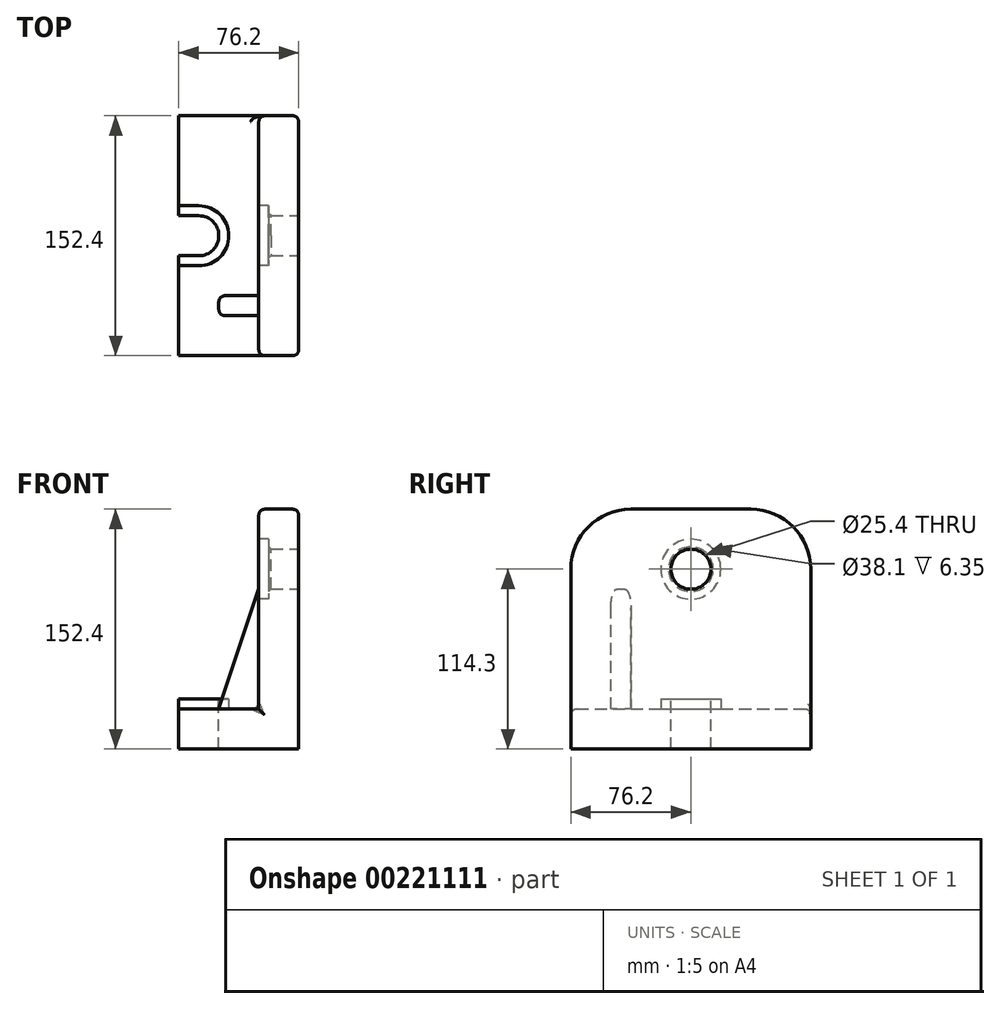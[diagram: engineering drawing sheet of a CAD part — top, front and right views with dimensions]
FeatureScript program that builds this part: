
annotation { "Feature Type Name" : "Feature", "Feature Type Description" : "" }
export const myFeature = defineFeature(function(context is Context, id is Id, definition is map)
    precondition{}
    {
        {
            var Q0;
            Q0=qCreatedBy(makeId("Front.planeOp"),FACE);
            var sketch = newSketch(context, id + "F0", { "sketchPlane" : qUnion([Q0])});
            skLineSegment(sketch, "E0", {"start": v(0, 0) * mm, "end": v(-76.2, 0) * mm});
            skLineSegment(sketch, "E1", {"start": v(-76.2, 0) * mm, "end": v(-76.2, 25.4) * mm});
            skLineSegment(sketch, "E2", {"start": v(-76.2, 25.4) * mm, "end": v(-25.4, 25.4) * mm});
            skLineSegment(sketch, "E3", {"start": v(-25.4, 25.4) * mm, "end": v(-25.4, 152.4) * mm});
            skLineSegment(sketch, "E4", {"start": v(-25.4, 152.4) * mm, "end": v(0, 152.4) * mm});
            skLineSegment(sketch, "E5", {"start": v(0, 152.4) * mm, "end": v(0, 0) * mm});
            skSolve(sketch);
        }
        {
            var Q0;
            Q0 = qSketchRegion(id + "F0", true);
            extrude(context, id + "F1", {"entities" : qUnion([Q0]), "endBound" : BoundingType.SYMMETRIC, "depth" : 152.4 * mm});
        }
        {
            var Q0;
            Q0=makeQuery(id+"F1.opExtrude","SWEPT_FACE",FACE,{"disambiguationData":[OSD([sQuery(id+"F0.wireOp",EDGE,"E5")])]});
            var sketch = newSketch(context, id + "F2", { "sketchPlane" : qUnion([Q0])});
            skCircle(sketch, "E6", {"center": v(0, 114.3) * mm, "radius": 12.7 * mm});
            skSolve(sketch);
        }
        {
            var Q0;
            Q0=makeQuery(id+"F2.imprint","IMPRINT",FACE,{"disambiguationData":[TD([[makeQuery(id+"F2.imprint","IMPRINT",EDGE,{"derivedFrom":sQuery(id+"F2.wireOp",EDGE,"E6")}),1.0]])]});
            var Q1;
            Q1=sQuery(id+"F2.wireOp",EDGE,"E6");
            extrude(context, id + "F3", {"entities" : qUnion([Q0]), "operationType" : NewBodyOperationType.REMOVE, "surfaceEntities" : qUnion([Q1]), "endBound" : BoundingType.THROUGH_ALL, "oppositeDirection" : true, "depth" : 25.4 * mm});
        }
        {
            var Q0;
            Q0=makeQuery(id+"F1.opExtrude","SWEPT_FACE",FACE,{"disambiguationData":[OSD([sQuery(id+"F0.wireOp",EDGE,"E2")])]});
            var sketch = newSketch(context, id + "F4", { "sketchPlane" : qUnion([Q0])});
            skArc(sketch, "E7", {"start": v(-63.5, -12.7) * mm, "mid": v(-50.8, 0) * mm, "end": v(-63.5, 12.7) * mm});
            skLineSegment(sketch, "E8", {"start": v(-76.2, 12.7) * mm, "end": v(-63.5, 12.7) * mm});
            skLineSegment(sketch, "E9", {"start": v(-63.5, -12.7) * mm, "end": v(-76.2, -12.7) * mm});
            skLineSegment(sketch, "E10", {"start": v(-76.2, -12.7) * mm, "end": v(-76.2, 12.7) * mm});
            skSolve(sketch);
        }
        {
            var Q0;
            Q0 = qSketchRegion(id + "F4", true);
            extrude(context, id + "F5", {"entities" : qUnion([Q0]), "operationType" : NewBodyOperationType.REMOVE, "endBound" : BoundingType.THROUGH_ALL, "oppositeDirection" : true, "depth" : 25.4 * mm});
        }
        {
            var Q0;
            Q0=makeQuery(id+"F1.opExtrude","SWEPT_FACE",FACE,{"disambiguationData":[OSD([sQuery(id+"F0.wireOp",EDGE,"E3")])]});
            var sketch = newSketch(context, id + "F6", { "sketchPlane" : qUnion([Q0])});
            skCircle(sketch, "E11", {"center": v(0, 114.3) * mm, "radius": 19.05 * mm});
            skSolve(sketch);
        }
        {
            var Q0;
            Q0 = qSketchRegion(id + "F6", true);
            extrude(context, id + "F7", {"entities" : qUnion([Q0]), "operationType" : NewBodyOperationType.REMOVE, "oppositeDirection" : true, "depth" : 6.35 * mm});
        }
        {
            var Q0;
            Q0=makeQuery(id+"F1.opExtrude","CAP_EDGE",EDGE,{"disambiguationData":[OSD([sQuery(id+"F0.wireOp",EDGE,"E4")])],"isStart":false});
            var Q1;
            Q1=makeQuery(id+"F1.opExtrude","CAP_EDGE",EDGE,{"disambiguationData":[OSD([sQuery(id+"F0.wireOp",EDGE,"E4")])],"isStart":true});
            fillet(context, id + "F8", {"entities" : qUnion([Q0, Q1]), "radius" : 38.1 * mm, "tangentPropagation" : true, "allowEdgeOverflow" : false});
        }
        {
            var Q0;
            Q0=qCreatedBy(makeId("Front.planeOp"),FACE);
            cPlane(context, id + "F9", {"entities" : qUnion([Q0]), "cplaneType" : CPlaneType.OFFSET, "offset" : 44.45 * mm, "width" : 152.4 * mm, "height" : 152.4 * mm});
        }
        {
            var Q0;
            Q0=qCreatedBy(id+"F9.planeOp",FACE);
            var sketch = newSketch(context, id + "F10", { "sketchPlane" : qUnion([Q0])});
            skLineSegment(sketch, "E12", {"start": v(-25.4, 25.4) * mm, "end": v(-25.4, 101.6) * mm});
            skLineSegment(sketch, "E13", {"start": v(-25.4, 101.6) * mm, "end": v(-50.8, 25.4) * mm});
            skLineSegment(sketch, "E14", {"start": v(-50.8, 25.4) * mm, "end": v(-25.4, 25.4) * mm});
            skSolve(sketch);
        }
        {
            var Q0;
            Q0=makeQuery(id+"F10.imprint","IMPRINT",FACE,{"disambiguationData":[TD([[makeQuery(id+"F10.imprint","IMPRINT",EDGE,{"derivedFrom":sQuery(id+"F10.wireOp",EDGE,"E12")}),1.0]])]});
            extrude(context, id + "F11", {"entities" : qUnion([Q0]), "operationType" : NewBodyOperationType.ADD, "endBound" : BoundingType.SYMMETRIC, "depth" : 12.7 * mm});
        }
        {
            var Q0;
            Q0=makeQuery(id+"F7.boolean.opBoolean","COPY",EDGE,{"derivedFrom":makeQuery(id+"F7.opExtrude","CAP_EDGE",EDGE,{"disambiguationData":[OSD([sQuery(id+"F6.wireOp",EDGE,"E11")])],"isStart":true})});
            var Q1;
            Q1=makeQuery(id+"F7.boolean.opBoolean","INTERSECT",EDGE,{"derivedFrom":[makeQuery(id+"F3.boolean.opBoolean","COPY",FACE,{"derivedFrom":makeQuery(id+"F3.opExtrude","SWEPT_FACE",FACE,{"disambiguationData":[OSD([sQuery(id+"F2.wireOp",EDGE,"E6")])]})}),makeQuery(id+"F7.opExtrude","CAP_FACE",FACE,{"disambiguationData":[OSD([sQuery(id+"F6.wireOp",EDGE,"E11")])],"isStart":false})]});
            chamfer(context, id + "F12", {"entities" : qUnion([Q0, Q1]), "width" : 1.52 * mm, "tangentPropagation" : true});
        }
        {
            var Q0;
            Q0=makeQuery(id+"F1.opExtrude","SWEPT_FACE",FACE,{"disambiguationData":[OSD([sQuery(id+"F0.wireOp",EDGE,"E2")])]});
            var sketch = newSketch(context, id + "F13", { "sketchPlane" : qUnion([Q0])});
            skLineSegment(sketch, "E15.0", {"start": v(-63.5, -19.05) * mm, "end": v(-76.2, -19.05) * mm});
            skArc(sketch, "E15.1", {"start": v(-63.5, -19.05) * mm, "mid": v(-44.45, 0) * mm, "end": v(-63.5, 19.05) * mm});
            skLineSegment(sketch, "E15.2", {"start": v(-76.2, 19.05) * mm, "end": v(-63.5, 19.05) * mm});
            skLineSegment(sketch, "E16.10", {"start": v(-69.85, 19.05) * mm, "end": v(-63.5, 19.05) * mm});
            skArc(sketch, "E16.11", {"start": v(-63.5, 19.05) * mm, "mid": v(-44.45, 0) * mm, "end": v(-63.5, -19.05) * mm});
            skLineSegment(sketch, "E16.12", {"start": v(-63.5, -19.05) * mm, "end": v(-69.85, -19.05) * mm});
            skLineSegment(sketch, "E17.0", {"start": v(-69.85, 12.7) * mm, "end": v(-63.5, 12.7) * mm});
            skLineSegment(sketch, "E18", {"start": v(-76.2, 19.05) * mm, "end": v(-76.2, 12.7) * mm});
            skLineSegment(sketch, "E19", {"start": v(-76.2, 12.7) * mm, "end": v(-69.85, 12.7) * mm});
            skLineSegment(sketch, "E20", {"start": v(-76.2, -19.05) * mm, "end": v(-76.2, -12.7) * mm});
            skLineSegment(sketch, "E21", {"start": v(-76.2, -12.7) * mm, "end": v(-63.5, -12.7) * mm});
            skArc(sketch, "E22", {"start": v(-63.5, -12.7) * mm, "mid": v(-50.8, 0) * mm, "end": v(-63.5, 12.7) * mm});
            skSolve(sketch);
        }
        {
            var Q0;
            Q0 = qSketchRegion(id + "F13", true);
            extrude(context, id + "F14", {"entities" : qUnion([Q0]), "operationType" : NewBodyOperationType.ADD, "depth" : 6.35 * mm});
        }
        {
            var Q0;
            Q0=makeQuery(id+"FMNxAku15RPFncp_1.1.F11.opExtrude","CAP_EDGE",EDGE,{"disambiguationData":[OSD([sQuery(id+"F10.wireOp",EDGE,"E12")])],"isStart":true});
            var Q1;
            Q1=makeQuery(id+"F11.opExtrude","CAP_EDGE",EDGE,{"disambiguationData":[OSD([sQuery(id+"F10.wireOp",EDGE,"E12")])],"isStart":false});
            var Q2;
            Q2=makeQuery(id+"F8.opFillet","BLEND_EDGE",EDGE,{"blendedFrom":[makeQuery(id+"F1.opExtrude","CAP_EDGE",EDGE,{"disambiguationData":[OSD([sQuery(id+"F0.wireOp",EDGE,"E4")])],"isStart":false}),makeQuery(id+"F1.opExtrude","SWEPT_FACE",FACE,{"disambiguationData":[OSD([sQuery(id+"F0.wireOp",EDGE,"E3")])]})],"blendedInto":[makeQuery(id+"F1.opExtrude","SWEPT_FACE",FACE,{"disambiguationData":[OSD([sQuery(id+"F0.wireOp",EDGE,"E3")])]})]});
            var Q3;
            Q3=makeQuery(id+"F8.opFillet","BLEND_EDGE",EDGE,{"blendedFrom":[makeQuery(id+"F1.opExtrude","CAP_EDGE",EDGE,{"disambiguationData":[OSD([sQuery(id+"F0.wireOp",EDGE,"E4")])],"isStart":false}),makeQuery(id+"F1.opExtrude","SWEPT_FACE",FACE,{"disambiguationData":[OSD([sQuery(id+"F0.wireOp",EDGE,"E5")])]})],"blendedInto":[makeQuery(id+"F1.opExtrude","SWEPT_FACE",FACE,{"disambiguationData":[OSD([sQuery(id+"F0.wireOp",EDGE,"E5")])]})]});
            var Q4;
            Q4=makeQuery(id+"F11.opExtrude","CAP_EDGE",EDGE,{"disambiguationData":[OSD([sQuery(id+"F10.wireOp",EDGE,"E13")])],"isStart":false});
            var Q5;
            Q5=makeQuery(id+"F11.opExtrude","CAP_EDGE",EDGE,{"disambiguationData":[OSD([sQuery(id+"F10.wireOp",EDGE,"E13")])],"isStart":true});
            var Q6;
            Q6=makeQuery(id+"FMNxAku15RPFncp_1.1.F11.opExtrude","CAP_EDGE",EDGE,{"disambiguationData":[OSD([sQuery(id+"F10.wireOp",EDGE,"E13")])],"isStart":true});
            var Q7;
            Q7=makeQuery(id+"FMNxAku15RPFncp_1.1.F11.opExtrude","CAP_EDGE",EDGE,{"disambiguationData":[OSD([sQuery(id+"F10.wireOp",EDGE,"E13")])],"isStart":false});
            var Q8;
            Q8=makeQuery(id+"F1.opExtrude","CAP_EDGE",EDGE,{"disambiguationData":[OSD([sQuery(id+"F0.wireOp",EDGE,"E2")])],"isStart":false});
            var Q9;
            Q9=makeQuery(id+"F1.opExtrude","CAP_EDGE",EDGE,{"disambiguationData":[OSD([sQuery(id+"F0.wireOp",EDGE,"E2")])],"isStart":true});
            var Q10;
            Q10=makeQuery(id+"F14.opExtrude","CAP_EDGE",EDGE,{"disambiguationData":[OSD([sQuery(id+"F13.wireOp",EDGE,"E15.0"),sQuery(id+"F13.wireOp",EDGE,"E16.12")])],"isStart":true});
            fillet(context, id + "F15", {"entities" : qUnion([Q0, Q1, Q2, Q3, Q4, Q5, Q6, Q7, Q8, Q9, Q10]), "radius" : 3.8 * mm, "tangentPropagation" : true, "allowEdgeOverflow" : false});
        }
        {
            var Q0;
            {var subQ0=sQuery(id+"F0.wireOp",EDGE,"E3");var subQ1=sQuery(id+"F0.wireOp",EDGE,"E2");var subQ5=sQuery(id+"F10.wireOp",EDGE,"E14");var subQ6=sQuery(id+"F10.wireOp",EDGE,"E13");var subQ7=sQuery(id+"F10.wireOp",EDGE,"E12");Q0=makeQuery(id+"FMNxAku15RPFncp_1.1.F11.boolean.opBoolean","SPLIT",EDGE,{"disambiguationData":[TD([makeQuery(id+"FMNxAku15RPFncp_1.1.F11.opExtrude","CAP_FACE",FACE,{"disambiguationData":[OSD([subQ7,subQ6,subQ5])],"isStart":false})])],"derivedFrom":makeQuery(id+"F11.boolean.opBoolean","SPLIT",EDGE,{"disambiguationData":[TD([makeQuery(id+"F11.opExtrude","CAP_FACE",FACE,{"disambiguationData":[OSD([subQ7,subQ6,subQ5])],"isStart":true})])],"derivedFrom":makeQuery(id+"F1.opExtrude","SWEPT_EDGE",EDGE,{"disambiguationData":[OSD([subQ1,subQ0])]})})});}
            fillet(context, id + "F16", {"entities" : qUnion([Q0]), "radius" : 5.08 * mm, "tangentPropagation" : true, "allowEdgeOverflow" : false});
        }
    });
